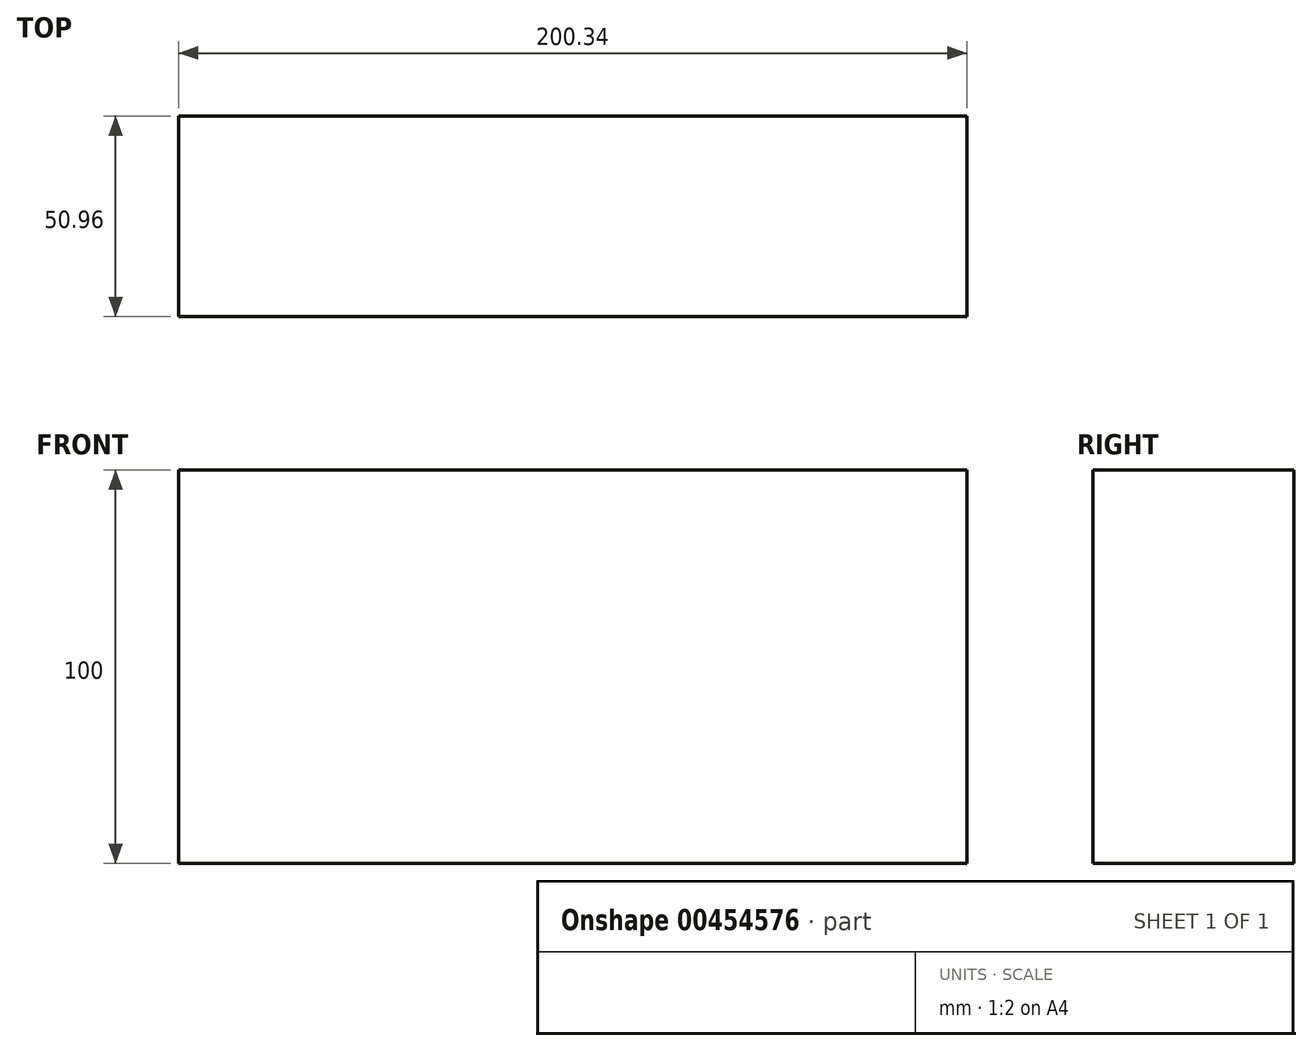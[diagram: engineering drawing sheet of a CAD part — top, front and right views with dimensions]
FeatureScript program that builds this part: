
annotation { "Feature Type Name" : "Feature", "Feature Type Description" : "" }
export const myFeature = defineFeature(function(context is Context, id is Id, definition is map)
    precondition{}
    {
        {
            var Q0;
            Q0=qCreatedBy(makeId("Top.planeOp"),FACE);
            var sketch = newSketch(context, id + "F0", { "sketchPlane" : qUnion([Q0])});
            skLineSegment(sketch, "E0.bottom", {"start": v(-111.92, 44.68) * mm, "end": v(88.42, 44.68) * mm});
            skLineSegment(sketch, "E0.top", {"start": v(-111.92, -6.28) * mm, "end": v(88.42, -6.28) * mm});
            skLineSegment(sketch, "E0.left", {"start": v(-111.92, 44.68) * mm, "end": v(-111.92, -6.28) * mm});
            skLineSegment(sketch, "E0.right", {"start": v(88.42, 44.68) * mm, "end": v(88.42, -6.28) * mm});
            skSolve(sketch);
        }
        {
            var Q0;
            Q0=makeQuery(id+"F0.imprint","IMPRINT",FACE,{"disambiguationData":[TD([[makeQuery(id+"F0.imprint","IMPRINT",EDGE,{"derivedFrom":sQuery(id+"F0.wireOp",EDGE,"E0.bottom")}),-1.0]])]});
            extrude(context, id + "F1", {"entities" : qUnion([Q0]), "depth" : 100 * mm});
        }
    });
